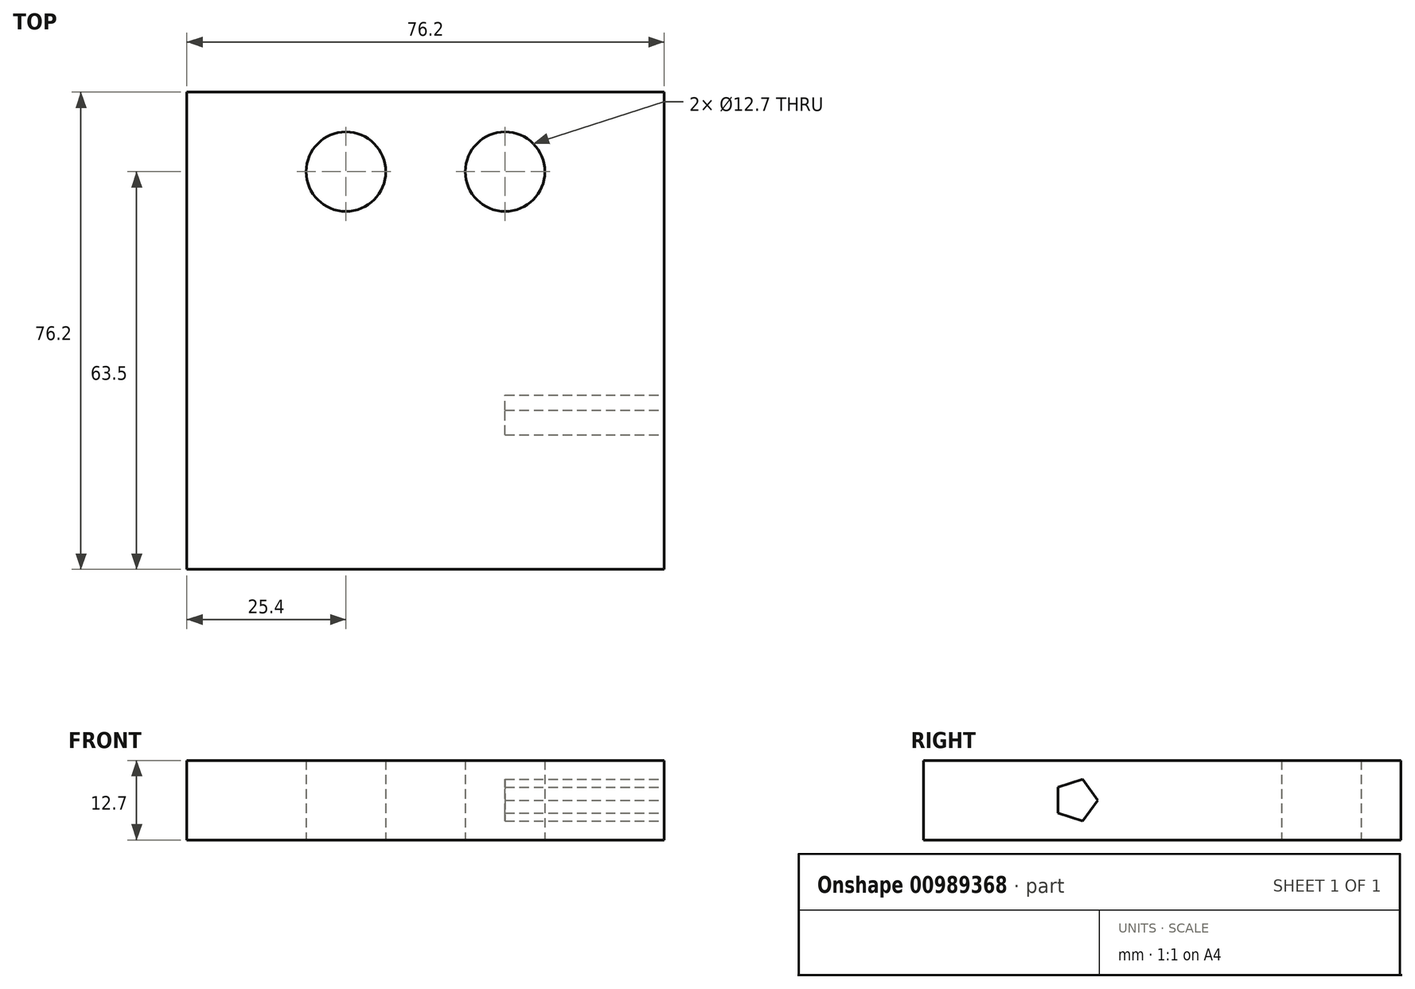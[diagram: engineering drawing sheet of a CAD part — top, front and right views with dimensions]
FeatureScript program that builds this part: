
annotation { "Feature Type Name" : "Feature", "Feature Type Description" : "" }
export const myFeature = defineFeature(function(context is Context, id is Id, definition is map)
    precondition{}
    {
        {
            var Q0;
            Q0=qCreatedBy(makeId("Top.planeOp"),FACE);
            var sketch = newSketch(context, id + "F0", { "sketchPlane" : qUnion([Q0])});
            skLineSegment(sketch, "E0.bottom", {"start": v(0, 0) * mm, "end": v(76.2, 0) * mm});
            skLineSegment(sketch, "E0.top", {"start": v(0, 76.2) * mm, "end": v(76.2, 76.2) * mm});
            skLineSegment(sketch, "E0.left", {"start": v(0, 0) * mm, "end": v(0, 76.2) * mm});
            skLineSegment(sketch, "E0.right", {"start": v(76.2, 0) * mm, "end": v(76.2, 76.2) * mm});
            skCircle(sketch, "E1", {"center": v(25.4, 63.5) * mm, "radius": 6.35 * mm});
            skCircle(sketch, "E2", {"center": v(50.8, 63.5) * mm, "radius": 6.35 * mm});
            skSolve(sketch);
        }
        {
            var Q0;
            Q0=makeQuery(id+"F0.imprint","IMPRINT",FACE,{"disambiguationData":[TD([[makeQuery(id+"F0.imprint","IMPRINT",EDGE,{"derivedFrom":sQuery(id+"F0.wireOp",EDGE,"E0.bottom")}),1.0]])]});
            extrude(context, id + "F1", {"entities" : qUnion([Q0]), "depth" : 12.7 * mm, "offsetDistance" : 25.4 * mm});
        }
        {
            var Q0;
            Q0=makeQuery(id+"F1.opExtrude","SWEPT_FACE",FACE,{"disambiguationData":[OSD([sQuery(id+"F0.wireOp",EDGE,"E0.right")])]});
            var sketch = newSketch(context, id + "F2", { "sketchPlane" : qUnion([Q0])});
            skCircle(sketch, "E3.cCircle", {"center": v(24.32, 6.35) * mm, "radius": 2.84 * mm, "construction": true});
            skLineSegment(sketch, "E3.0", {"start": v(25.4, 9.69) * mm, "end": v(27.83, 6.35) * mm});
            skLineSegment(sketch, "E3.1", {"start": v(27.83, 6.35) * mm, "end": v(25.4, 3.01) * mm});
            skLineSegment(sketch, "E3.2", {"start": v(25.4, 3.01) * mm, "end": v(21.48, 4.29) * mm});
            skLineSegment(sketch, "E3.3", {"start": v(21.48, 4.29) * mm, "end": v(21.48, 8.41) * mm});
            skLineSegment(sketch, "E3.4", {"start": v(21.48, 8.41) * mm, "end": v(25.4, 9.69) * mm});
            skPoint(sketch, "E3.0.midPoint", {"position": v(26.61, 8.02) * mm});
            skSolve(sketch);
        }
        {
            var Q0;
            Q0=makeQuery(id+"F2.imprint","IMPRINT",FACE,{"disambiguationData":[TD([[makeQuery(id+"F2.imprint","IMPRINT",EDGE,{"derivedFrom":sQuery(id+"F2.wireOp",EDGE,"E3.0")}),-1.0]])]});
            extrude(context, id + "F3", {"entities" : qUnion([Q0]), "operationType" : NewBodyOperationType.REMOVE, "oppositeDirection" : true, "depth" : 25.4 * mm, "offsetDistance" : 25.4 * mm});
        }
    });
